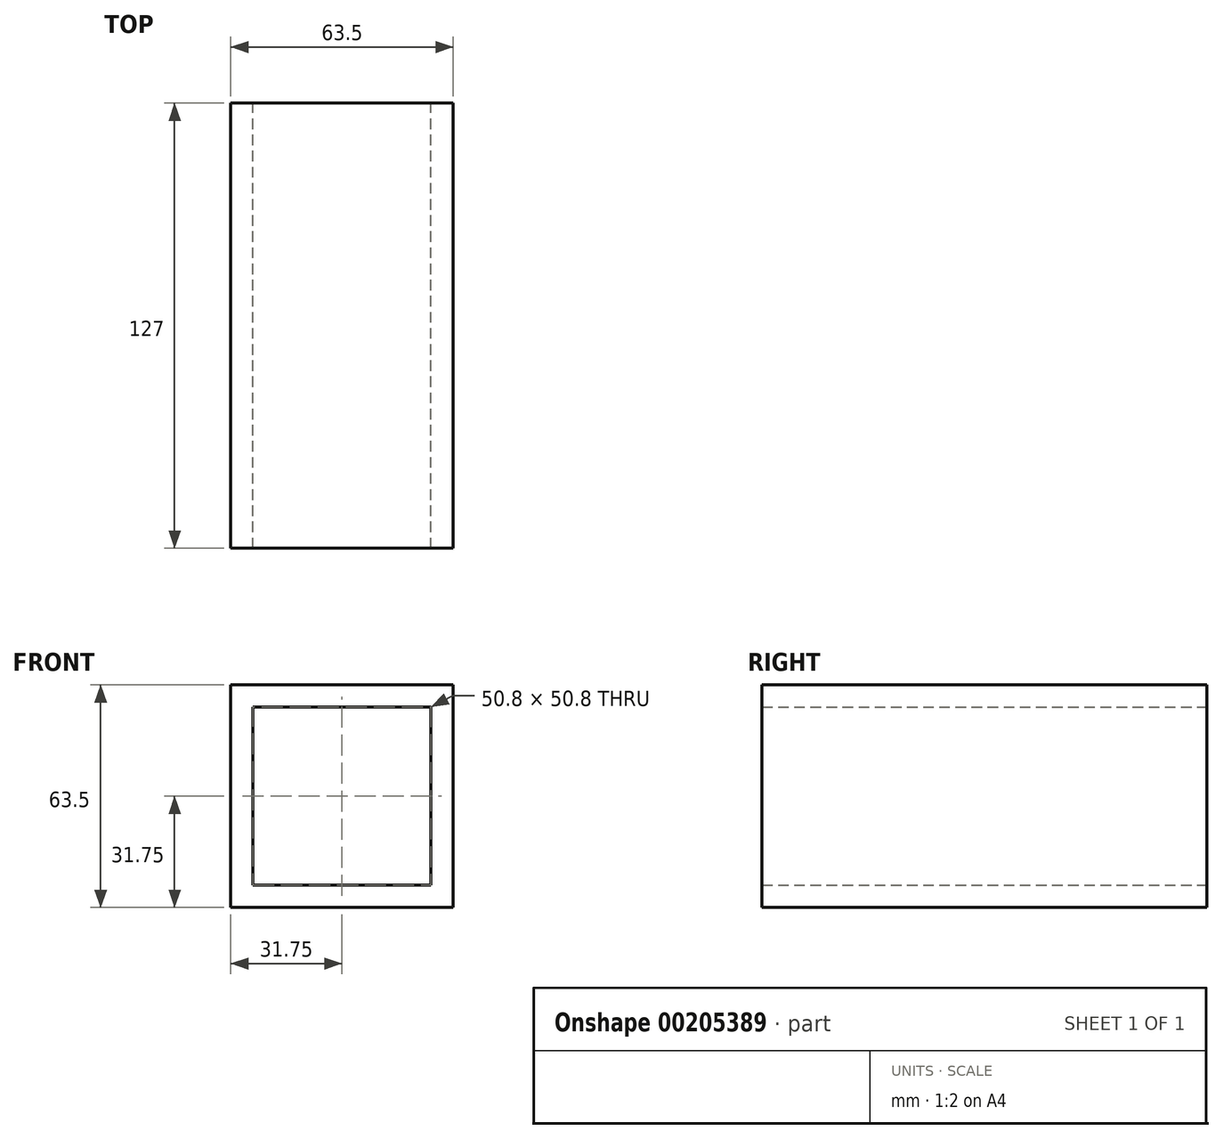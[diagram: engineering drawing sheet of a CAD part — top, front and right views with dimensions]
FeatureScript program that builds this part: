
annotation { "Feature Type Name" : "Feature", "Feature Type Description" : "" }
export const myFeature = defineFeature(function(context is Context, id is Id, definition is map)
    precondition{}
    {
        {
            var Q0;
            Q0=qCreatedBy(makeId("Front.planeOp"),FACE);
            var sketch = newSketch(context, id + "F0", { "sketchPlane" : qUnion([Q0])});
            skLineSegment(sketch, "E0.bottom", {"start": v(31.75, 31.75) * mm, "end": v(-31.75, 31.75) * mm});
            skLineSegment(sketch, "E0.top", {"start": v(31.75, -31.75) * mm, "end": v(-31.75, -31.75) * mm});
            skLineSegment(sketch, "E0.left", {"start": v(31.75, 31.75) * mm, "end": v(31.75, -31.75) * mm});
            skLineSegment(sketch, "E0.right", {"start": v(-31.75, 31.75) * mm, "end": v(-31.75, -31.75) * mm});
            skPoint(sketch, "E0.middle", {"position": v(0, 0) * mm});
            skSolve(sketch);
        }
        {
            var Q0;
            Q0=makeQuery(id+"F0.imprint","IMPRINT",FACE,{"disambiguationData":[TD([[makeQuery(id+"F0.imprint","IMPRINT",EDGE,{"derivedFrom":sQuery(id+"F0.wireOp",EDGE,"E0.bottom")}),1.0]])]});
            extrude(context, id + "F1", {"entities" : qUnion([Q0]), "depth" : 127 * mm});
        }
        {
            var Q0;
            Q0=makeQuery(id+"F1.opExtrude","CAP_FACE",FACE,{"disambiguationData":[OSD([sQuery(id+"F0.wireOp",EDGE,"E0.bottom"),sQuery(id+"F0.wireOp",EDGE,"E0.top"),sQuery(id+"F0.wireOp",EDGE,"E0.left"),sQuery(id+"F0.wireOp",EDGE,"E0.right")])],"isStart":true});
            var sketch = newSketch(context, id + "F2", { "sketchPlane" : qUnion([Q0])});
            skLineSegment(sketch, "E1.bottom", {"start": v(25.4, 25.4) * mm, "end": v(-25.4, 25.4) * mm});
            skLineSegment(sketch, "E1.top", {"start": v(25.4, -25.4) * mm, "end": v(-25.4, -25.4) * mm});
            skLineSegment(sketch, "E1.left", {"start": v(25.4, 25.4) * mm, "end": v(25.4, -25.4) * mm});
            skLineSegment(sketch, "E1.right", {"start": v(-25.4, 25.4) * mm, "end": v(-25.4, -25.4) * mm});
            skPoint(sketch, "E1.middle", {"position": v(0, 0) * mm});
            skSolve(sketch);
        }
        {
            var Q0;
            Q0 = qSketchRegion(id + "F2", true);
            extrude(context, id + "F3", {"entities" : qUnion([Q0]), "operationType" : NewBodyOperationType.REMOVE, "oppositeDirection" : true, "depth" : 127 * mm});
        }
    });
